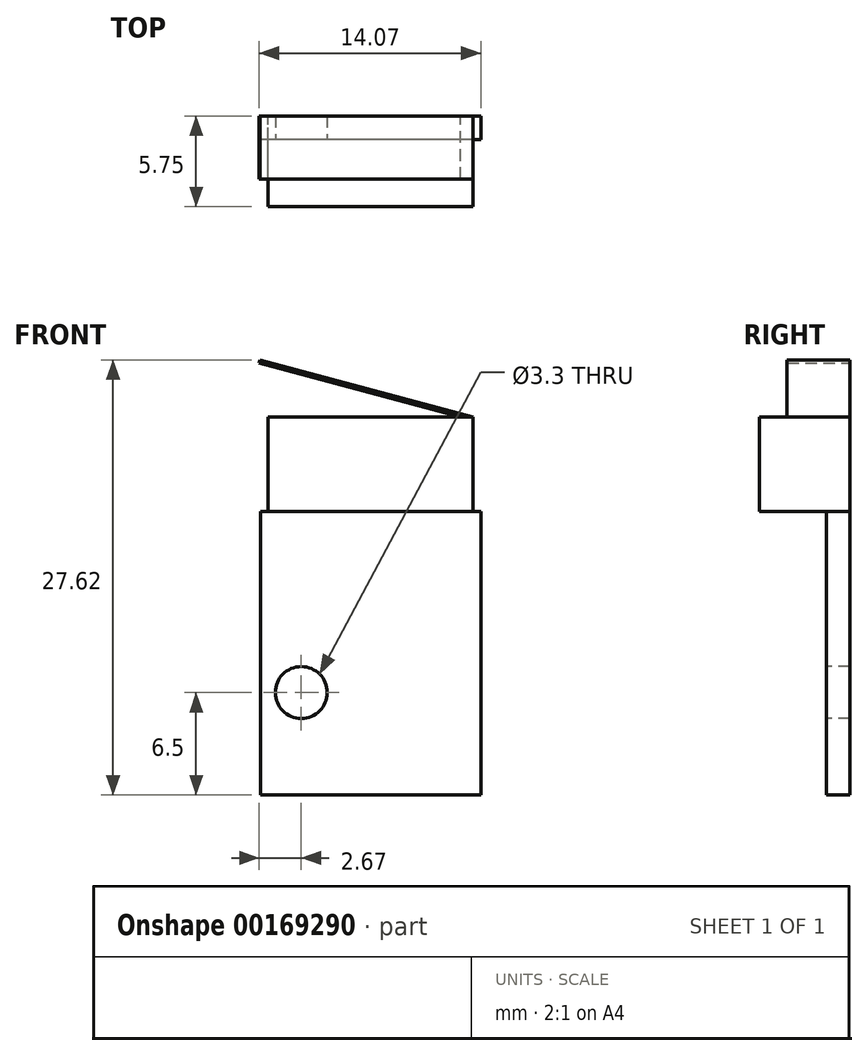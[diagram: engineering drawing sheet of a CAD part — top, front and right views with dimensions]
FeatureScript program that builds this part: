
annotation { "Feature Type Name" : "Feature", "Feature Type Description" : "" }
export const myFeature = defineFeature(function(context is Context, id is Id, definition is map)
    precondition{}
    {
        {
            var Q0;
            Q0=qCreatedBy(makeId("Top.planeOp"),FACE);
            var sketch = newSketch(context, id + "F0", { "sketchPlane" : qUnion([Q0])});
            skLineSegment(sketch, "E0.bottom", {"start": v(7, 9) * mm, "end": v(-7, 9) * mm});
            skLineSegment(sketch, "E0.top", {"start": v(7, -9) * mm, "end": v(-7, -9) * mm});
            skLineSegment(sketch, "E0.left", {"start": v(7, 9) * mm, "end": v(7, -9) * mm});
            skLineSegment(sketch, "E0.right", {"start": v(-7, 9) * mm, "end": v(-7, -9) * mm});
            skPoint(sketch, "E0.middle", {"position": v(0, 0) * mm});
            skSolve(sketch);
        }
        {
            var Q0;
            Q0=makeQuery(id+"F0.imprint","IMPRINT",FACE,{"disambiguationData":[TD([[makeQuery(id+"F0.imprint","IMPRINT",EDGE,{"derivedFrom":sQuery(id+"F0.wireOp",EDGE,"E0.bottom")}),1.0]])]});
            extrude(context, id + "F1", {"entities" : qUnion([Q0]), "depth" : 1.5 * mm});
        }
        {
            var Q0;
            Q0=qCreatedBy(makeId("Top.planeOp"),FACE);
            var sketch = newSketch(context, id + "F2", { "sketchPlane" : qUnion([Q0])});
            skLineSegment(sketch, "E1.bottom", {"start": v(-6.5, 15) * mm, "end": v(6.5, 15) * mm});
            skLineSegment(sketch, "E1.top", {"start": v(-6.5, 9) * mm, "end": v(6.5, 9) * mm});
            skLineSegment(sketch, "E1.left", {"start": v(-6.5, 15) * mm, "end": v(-6.5, 9) * mm});
            skLineSegment(sketch, "E1.right", {"start": v(6.5, 15) * mm, "end": v(6.5, 9) * mm});
            skLineSegment(sketch, "E2", {"start": v(0, 15) * mm, "end": v(0, 9) * mm, "construction": true});
            skSolve(sketch);
        }
        {
            var Q0;
            Q0 = qSketchRegion(id + "F2", true);
            extrude(context, id + "F3", {"entities" : qUnion([Q0]), "operationType" : NewBodyOperationType.ADD, "depth" : 5.75 * mm});
        }
        {
            var Q0;
            Q0=makeQuery(id+"F1.opExtrude","CAP_FACE",FACE,{"disambiguationData":[OSD([sQuery(id+"F0.wireOp",EDGE,"E0.bottom"),sQuery(id+"F0.wireOp",EDGE,"E0.top"),sQuery(id+"F0.wireOp",EDGE,"E0.left"),sQuery(id+"F0.wireOp",EDGE,"E0.right")])],"isStart":false});
            var sketch = newSketch(context, id + "F4", { "sketchPlane" : qUnion([Q0])});
            skCircle(sketch, "E3", {"center": v(-4.4, -2.5) * mm, "radius": 1.65 * mm});
            skSolve(sketch);
        }
        {
            var Q0;
            Q0 = qSketchRegion(id + "F4", true);
            extrude(context, id + "F5", {"entities" : qUnion([Q0]), "operationType" : NewBodyOperationType.REMOVE, "oppositeDirection" : true, "depth" : 25 * mm});
        }
        {
            var Q0;
            Q0=qCreatedBy(makeId("Top.planeOp"),FACE);
            var sketch = newSketch(context, id + "F6", { "sketchPlane" : qUnion([Q0])});
            skLineSegment(sketch, "E4", {"start": v(6.5, 15) * mm, "end": v(-7.02, 18.62) * mm});
            skLineSegment(sketch, "E5", {"start": v(-7.02, 18.62) * mm, "end": v(-7.07, 18.43) * mm});
            skLineSegment(sketch, "E6", {"start": v(-7.07, 18.43) * mm, "end": v(5.73, 15) * mm});
            skLineSegment(sketch, "E7", {"start": v(5.73, 15) * mm, "end": v(6.5, 15) * mm});
            skSolve(sketch);
        }
        {
            var Q0;
            Q0 = qSketchRegion(id + "F6", true);
            extrude(context, id + "F7", {"entities" : qUnion([Q0]), "operationType" : NewBodyOperationType.ADD, "depth" : 4 * mm});
        }
        {
            var Q0;
            Q0=makeQuery(id+"F1.opExtrude","SWEPT_BODY",BODY,{"disambiguationData":[OSD([sQuery(id+"F0.wireOp",EDGE,"E0.bottom"),sQuery(id+"F0.wireOp",EDGE,"E0.top"),sQuery(id+"F0.wireOp",EDGE,"E0.left"),sQuery(id+"F0.wireOp",EDGE,"E0.right")])]});
            var Q1;
            Q1=makeQuery(id+"F1.opExtrude","CAP_EDGE",EDGE,{"disambiguationData":[OSD([sQuery(id+"F0.wireOp",EDGE,"E0.top")])],"isStart":false});
            transform(context, id + "F8", {"entities" : qUnion([Q0]), "transformType" : TransformType.ROTATION, "transformAxis" : qUnion([Q1]), "angle" : 90 * degree, "oppositeDirection" : true, "makeCopy" : false});
        }
        {
            var Q0;
            Q0=makeQuery(id+"F1.opExtrude","SWEPT_BODY",BODY,{"disambiguationData":[OSD([sQuery(id+"F0.wireOp",EDGE,"E0.bottom"),sQuery(id+"F0.wireOp",EDGE,"E0.top"),sQuery(id+"F0.wireOp",EDGE,"E0.left"),sQuery(id+"F0.wireOp",EDGE,"E0.right")])]});
            transform(context, id + "F9", {"entities" : qUnion([Q0]), "transformType" : TransformType.TRANSLATION_3D, "dx" : 0 * mm, "dy" : -6 * mm, "dz" : -17.7 * mm, "makeCopy" : false});
        }
    });
